# Revit family: Paging Station-Surface Mounted-Q-SYS-PS-TSCG3-G-Gooseneck Microphone z
name_source: partatom
category: Communication Devices
units: mm (PartAtom-declared; Revit-internal decimal feet)

## family parameters
Cut with Voids When Loaded = No
Host = Face
Maintain Annotation Orientation = No
OmniClass Number = 23.85.10.17.11
OmniClass Title = Audio-Visual System Components
Part Type = Normal
Room Calculation Point = No
Round Connector Dimension = Use Diameter
Shared = No

## types (1)
- 10 " W x 5 " H x 2 " D
    Body Depth = 17 mm
    Body Material = Plastic - Q-SYS - Black
    Body Offset = 0 mm  [stored 0 ft]
    Body Width = 265.8 mm  [stored 0.872047 ft]
    Cord Material 1 = Plastic - Q-SYS - Black Cord 1
    Default Elevation = 1450 mm
    Depth = 113.7 mm  [stored 0.373031 ft]
    Description = Surface mounted paging station with gooseneck microphone and an integrated push-to-talk button.
    Frame Depth = 2 mm  [stored 0.00656168 ft]
    Height = 86.4 mm  [stored 0.283465 ft]
    Highlight Material = Metal - Q-SYS - Mesh
    IQ Category = Paging Station
    LED Material = Plastic - Q-SYS - LED Blue
    Length 1 = 5 mm  [stored 0.0164042 ft]
    Length 2 = 55 mm
    Length 3 = 7 mm
    Length 4 = 0.5 mm  [stored 0.00164042 ft]
    Length 5 = 11 mm
    Manufacturer = Q-SYS
    Manufacturer URL = https://www.qsys.com
    Model = PS-TSCG3-H
    Product Documentation Link = https://www.qsys.com
    Product Page URL = https://www.qsys.com
    Screen Height = 115.6 mm
    Type Comments = 10 " W x 5 " H x 2 " D
    URL = https://www.qsys.com
    Weight = 3.99 lbm
    Weight Dimensional = 1.84
    Weight Product = 1.18
    Width = 265.8 mm  [stored 0.872047 ft]

note: [stored X ft] marks values corroborated as IEEE doubles in the binary element streams (Revit-internal decimal feet)

## geometry (parser evidence)
native form markers: Sweep x2
no freeform markers — native parametric forms only
